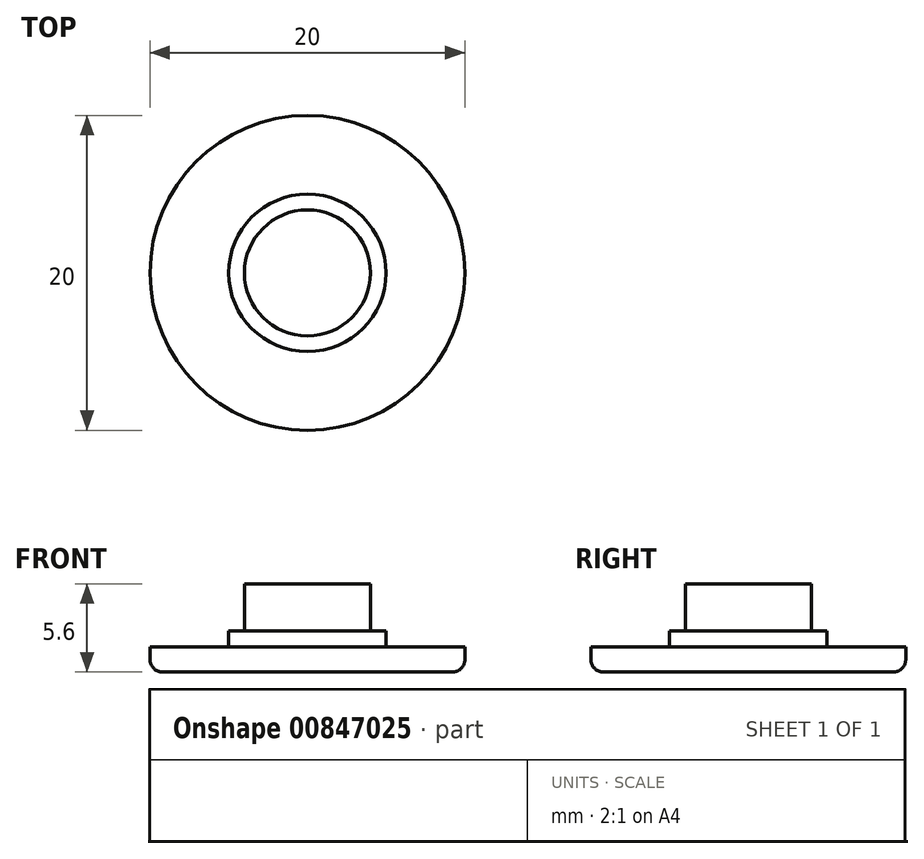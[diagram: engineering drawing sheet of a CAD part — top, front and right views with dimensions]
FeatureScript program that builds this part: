
annotation { "Feature Type Name" : "Feature", "Feature Type Description" : "" }
export const myFeature = defineFeature(function(context is Context, id is Id, definition is map)
    precondition{}
    {
        {
            var Q0;
            Q0=qCreatedBy(makeId("Top.planeOp"),FACE);
            var sketch = newSketch(context, id + "F0", { "sketchPlane" : qUnion([Q0])});
            skCircle(sketch, "E0", {"center": v(0, 0) * mm, "radius": 10 * mm});
            skSolve(sketch);
        }
        {
            var Q0;
            Q0=makeQuery(id+"F0.imprint","IMPRINT",FACE,{"disambiguationData":[TD([[makeQuery(id+"F0.imprint","IMPRINT",EDGE,{"derivedFrom":sQuery(id+"F0.wireOp",EDGE,"E0")}),1.0]])]});
            extrude(context, id + "F1", {"entities" : qUnion([Q0]), "depth" : 1.6 * mm, "offsetDistance" : 25 * mm});
        }
        {
            var Q0;
            Q0=makeQuery(id+"F1.opExtrude","CAP_FACE",FACE,{"disambiguationData":[OSD([sQuery(id+"F0.wireOp",EDGE,"E0")])],"isStart":false});
            var sketch = newSketch(context, id + "F2", { "sketchPlane" : qUnion([Q0])});
            skCircle(sketch, "E1", {"center": v(0, 0) * mm, "radius": 5 * mm});
            skSolve(sketch);
        }
        {
            var Q0;
            Q0=makeQuery(id+"F2.imprint","IMPRINT",FACE,{"disambiguationData":[TD([[makeQuery(id+"F2.imprint","IMPRINT",EDGE,{"derivedFrom":sQuery(id+"F2.wireOp",EDGE,"E1")}),1.0]])]});
            extrude(context, id + "F3", {"entities" : qUnion([Q0]), "operationType" : NewBodyOperationType.ADD, "depth" : 1 * mm, "offsetDistance" : 25 * mm});
        }
        {
            var Q0;
            Q0=makeQuery(id+"F3.opExtrude","CAP_FACE",FACE,{"disambiguationData":[OSD([sQuery(id+"F2.wireOp",EDGE,"E1")])],"isStart":false});
            var sketch = newSketch(context, id + "F4", { "sketchPlane" : qUnion([Q0])});
            skCircle(sketch, "E2", {"center": v(0, 0) * mm, "radius": 4 * mm});
            skSolve(sketch);
        }
        {
            var Q0;
            Q0=makeQuery(id+"F4.imprint","IMPRINT",FACE,{"disambiguationData":[TD([[makeQuery(id+"F4.imprint","IMPRINT",EDGE,{"derivedFrom":sQuery(id+"F4.wireOp",EDGE,"E2")}),1.0]])]});
            extrude(context, id + "F5", {"entities" : qUnion([Q0]), "depth" : 3 * mm, "offsetDistance" : 25 * mm});
        }
        {
            var Q0;
            Q0=makeQuery(id+"F1.opExtrude","CAP_EDGE",EDGE,{"disambiguationData":[OSD([sQuery(id+"F0.wireOp",EDGE,"E0")])],"isStart":true});
            fillet(context, id + "F6", {"entities" : qUnion([Q0]), "radius" : .8 * mm, "tangentPropagation" : true, "allowEdgeOverflow" : false});
        }
    });
